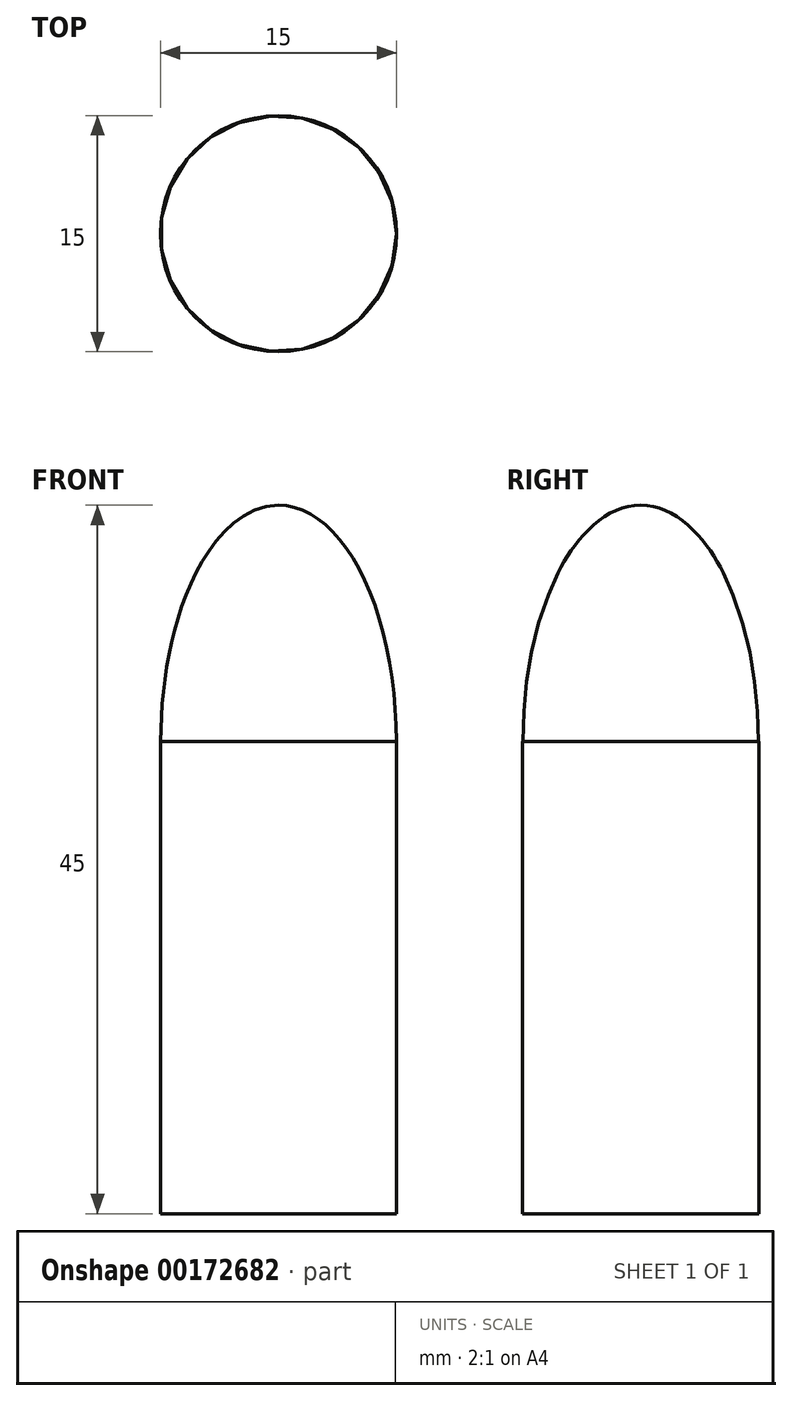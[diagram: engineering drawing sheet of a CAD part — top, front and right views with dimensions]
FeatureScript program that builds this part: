
annotation { "Feature Type Name" : "Feature", "Feature Type Description" : "" }
export const myFeature = defineFeature(function(context is Context, id is Id, definition is map)
    precondition{}
    {
        {
            var Q0;
            Q0=qCreatedBy(makeId("Front.planeOp"),FACE);
            var sketch = newSketch(context, id + "F0", { "sketchPlane" : qUnion([Q0])});
            skLineSegment(sketch, "E0.bottom", {"start": v(0, 0) * mm, "end": v(-7.5, 0) * mm});
            skLineSegment(sketch, "E0.top", {"start": v(0, 30) * mm, "end": v(-7.5, 30) * mm});
            skLineSegment(sketch, "E0.left", {"start": v(0, 0) * mm, "end": v(0, 30) * mm});
            skLineSegment(sketch, "E0.right", {"start": v(-7.5, 0) * mm, "end": v(-7.5, 30) * mm});
            skSolve(sketch);
        }
        {
            var Q0;
            Q0=qCreatedBy(makeId("Front.planeOp"),FACE);
            var sketch = newSketch(context, id + "F1", { "sketchPlane" : qUnion([Q0])});
            skEllipticalArc(sketch, "E1", {});
            skLineSegment(sketch, "E2", {"start": v(-7.5, 30) * mm, "end": v(-7.5, 45) * mm});
            skLineSegment(sketch, "E3", {"start": v(-7.5, 30) * mm, "end": v(-0.02, 30) * mm});
            const initialGuessF1  = {"E1": [-0.0075, 0.03, 0, 1, 0.015, 0.0074839754007557345, 4.71238898038469, 0]};
            skSetInitialGuess(sketch, initialGuessF1);
            skSolve(sketch);
        }
        {
            var Q0;
            Q0=makeQuery(id+"F1.imprint","IMPRINT",FACE,{"disambiguationData":[TD([[makeQuery(id+"F1.imprint","IMPRINT",EDGE,{"derivedFrom":sQuery(id+"F1.wireOp",EDGE,"E1")}),1.0]])]});
            var Q1;
            Q1=makeQuery(id+"F0.imprint","IMPRINT",FACE,{"disambiguationData":[TD([[makeQuery(id+"F0.imprint","IMPRINT",EDGE,{"derivedFrom":sQuery(id+"F0.wireOp",EDGE,"E0.bottom")}),-1.0]])]});
            var Q2;
            Q2=sQuery(id+"F1.wireOp",EDGE,"E2");
            revolve(context, id + "F2", {"entities" : qUnion([Q0, Q1]), "axis" : qUnion([Q2]), "revolveType" : RevolveType.FULL});
        }
    });
